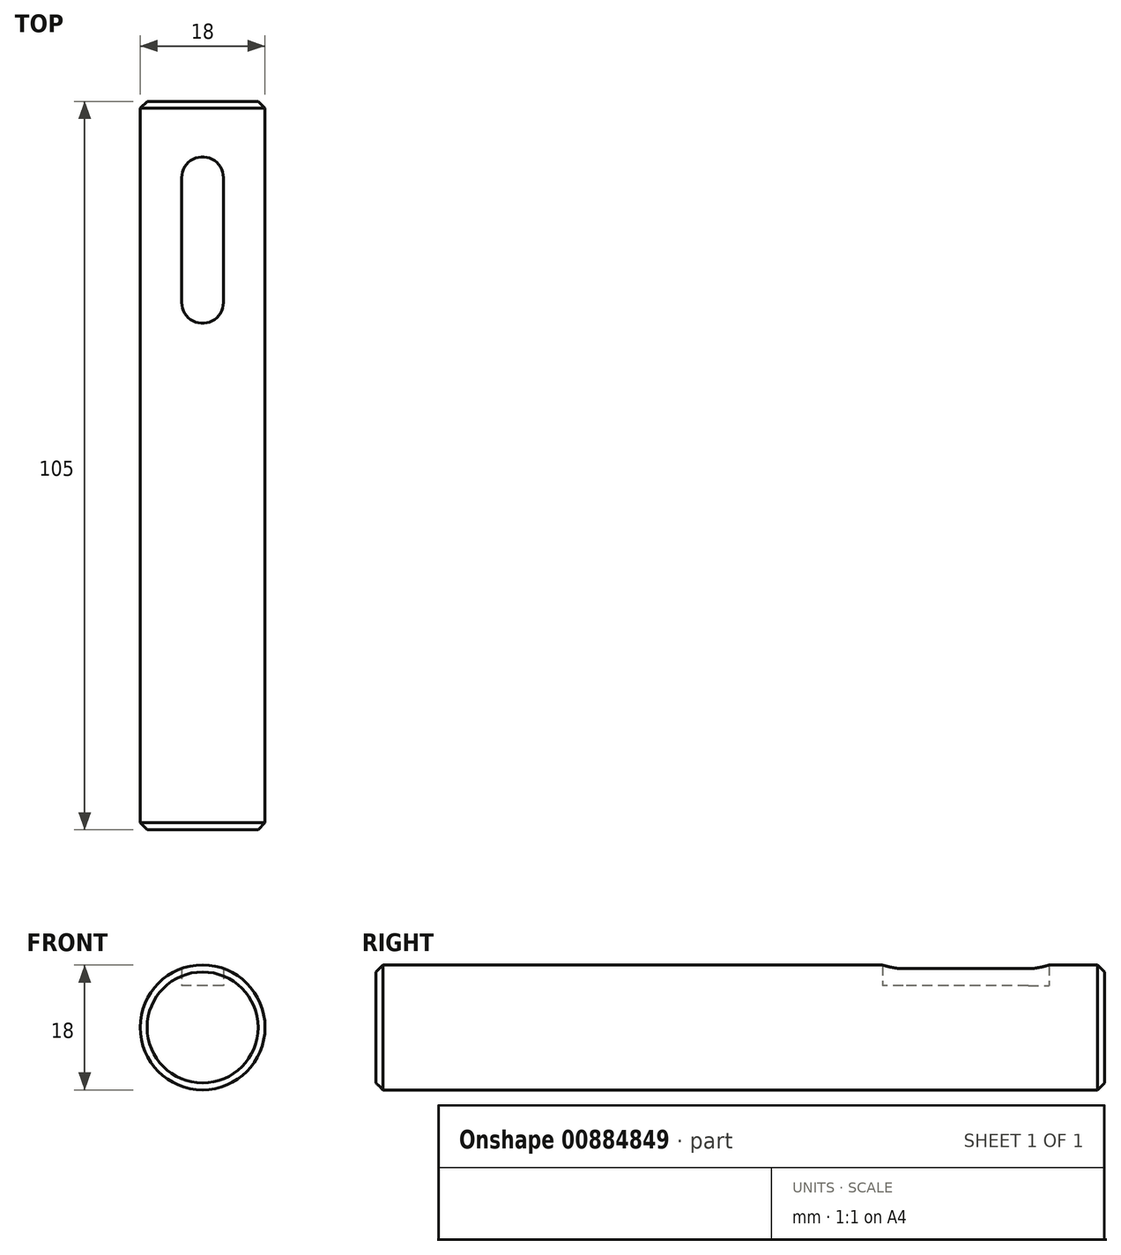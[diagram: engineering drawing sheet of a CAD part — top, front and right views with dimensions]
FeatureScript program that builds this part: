
annotation { "Feature Type Name" : "Feature", "Feature Type Description" : "" }
export const myFeature = defineFeature(function(context is Context, id is Id, definition is map)
    precondition{}
    {
        {
            var Q0;
            Q0=qCreatedBy(makeId("Front.planeOp"),FACE);
            var sketch = newSketch(context, id + "F0", { "sketchPlane" : qUnion([Q0])});
            skCircle(sketch, "E0", {"center": v(0, 0) * mm, "radius": 9 * mm});
            skSolve(sketch);
        }
        {
            var Q0;
            Q0 = qSketchRegion(id + "F0", true);
            extrude(context, id + "F1", {"entities" : qUnion([Q0]), "depth" : 105 * mm, "offsetDistance" : 25 * mm});
        }
        {
            var Q0;
            Q0=makeQuery(id+"F1.opExtrude","SWEPT_FACE",FACE,{"disambiguationData":[OSD([sQuery(id+"F0.wireOp",EDGE,"E0")])]});
            chamfer(context, id + "F2", {"entities" : qUnion([Q0]), "width" : 1 * mm, "tangentPropagation" : true});
        }
        {
            var Q0;
            Q0=qCreatedBy(makeId("Top.planeOp"),FACE);
            cPlane(context, id + "F3", {"entities" : qUnion([Q0]), "cplaneType" : CPlaneType.OFFSET, "offset" : 6 * mm, "width" : 150 * mm, "height" : 150 * mm});
        }
        {
            var Q0;
            Q0=qCreatedBy(id+"F3.planeOp",FACE);
            var sketch = newSketch(context, id + "F4", { "sketchPlane" : qUnion([Q0])});
            skLineSegment(sketch, "E1", {"start": v(0, -29) * mm, "end": v(0, 115.26) * mm, "construction": true});
            skArc(sketch, "E2", {"start": v(3, -11) * mm, "mid": v(0, -8) * mm, "end": v(-3, -11) * mm});
            skArc(sketch, "E3", {"start": v(-3, -29) * mm, "mid": v(0, -32) * mm, "end": v(3, -29) * mm});
            skLineSegment(sketch, "E4", {"start": v(-3, -11) * mm, "end": v(-3, -29) * mm});
            skLineSegment(sketch, "E5.MirrorCS", {"start": v(3, -11) * mm, "end": v(3, -29) * mm});
            skSolve(sketch);
        }
        {
            var Q0;
            Q0 = qSketchRegion(id + "F4", true);
            extrude(context, id + "F5", {"entities" : qUnion([Q0]), "operationType" : NewBodyOperationType.REMOVE, "depth" : 25 * mm, "offsetDistance" : 25 * mm});
        }
    });
